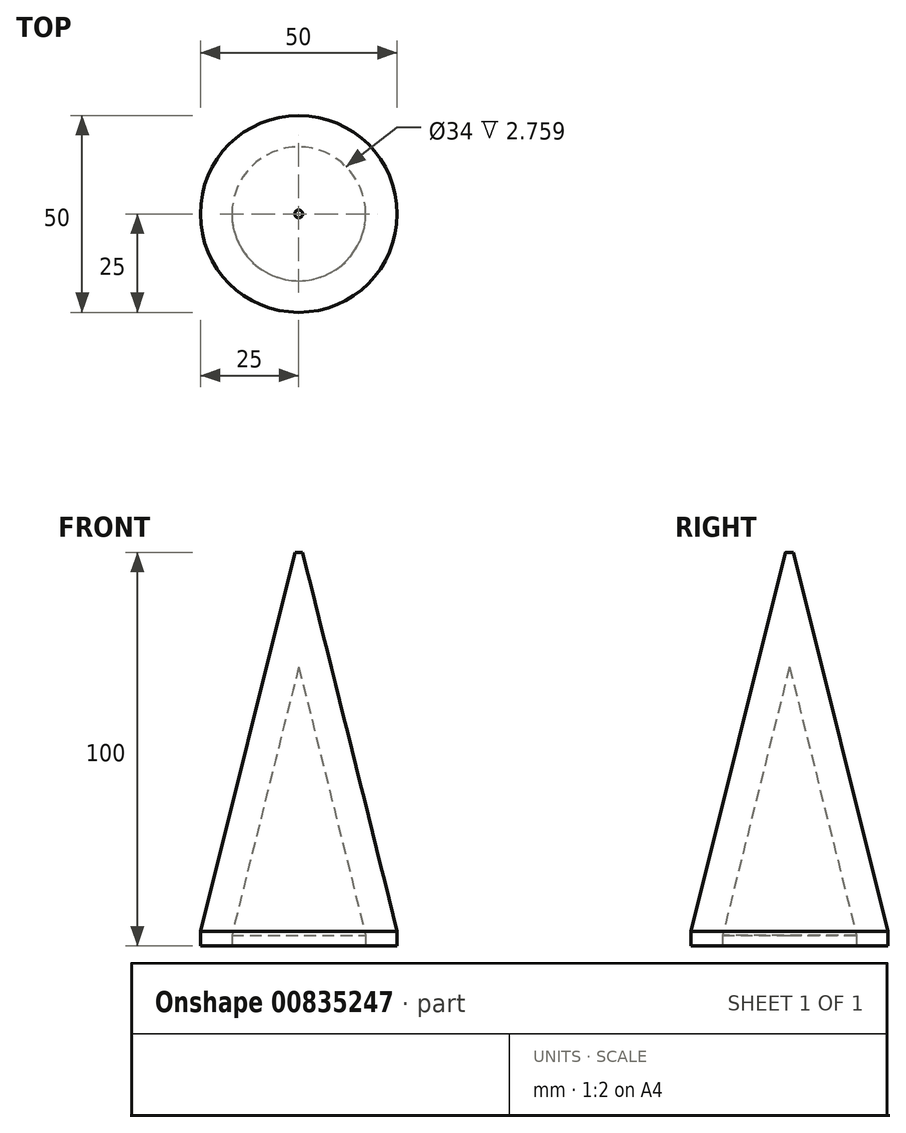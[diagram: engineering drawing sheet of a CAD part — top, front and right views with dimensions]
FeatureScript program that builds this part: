
annotation { "Feature Type Name" : "Feature", "Feature Type Description" : "" }
export const myFeature = defineFeature(function(context is Context, id is Id, definition is map)
    precondition{}
    {
        {
            var Q0;
            Q0=qCreatedBy(makeId("Top.planeOp"),FACE);
            var sketch = newSketch(context, id + "F0", { "sketchPlane" : qUnion([Q0])});
            skCircle(sketch, "E0", {"center": v(0, 0) * mm, "radius": 25 * mm});
            skSolve(sketch);
        }
        {
            var Q0;
            Q0=makeQuery(id+"F0.imprint","IMPRINT",FACE,{"disambiguationData":[TD([[makeQuery(id+"F0.imprint","IMPRINT",EDGE,{"derivedFrom":sQuery(id+"F0.wireOp",EDGE,"E0")}),1.0]])]});
            extrude(context, id + "F1", {"entities" : qUnion([Q0]), "depth" : 100 * mm, "offsetDistance" : 25 * mm});
        }
        {
            var Q0;
            Q0=makeQuery(id+"F1.opExtrude","CAP_FACE",FACE,{"disambiguationData":[OSD([sQuery(id+"F0.wireOp",EDGE,"E0")])],"isStart":false});
            chamfer(context, id + "F2", {"entities" : qUnion([Q0]), "chamferType" : ChamferType.OFFSET_ANGLE, "width" : 24 * mm, "oppositeDirection" : false, "angle" : 76 * degree, "tangentPropagation" : true});
        }
        {
            var Q0;
            Q0=makeQuery(id+"F1.opExtrude","CAP_FACE",FACE,{"disambiguationData":[OSD([sQuery(id+"F0.wireOp",EDGE,"E0")])],"isStart":true});
            shell(context, id + "F3", {"entities" : qUnion([Q0]), "thickness" : 8 * mm});
        }
    });
